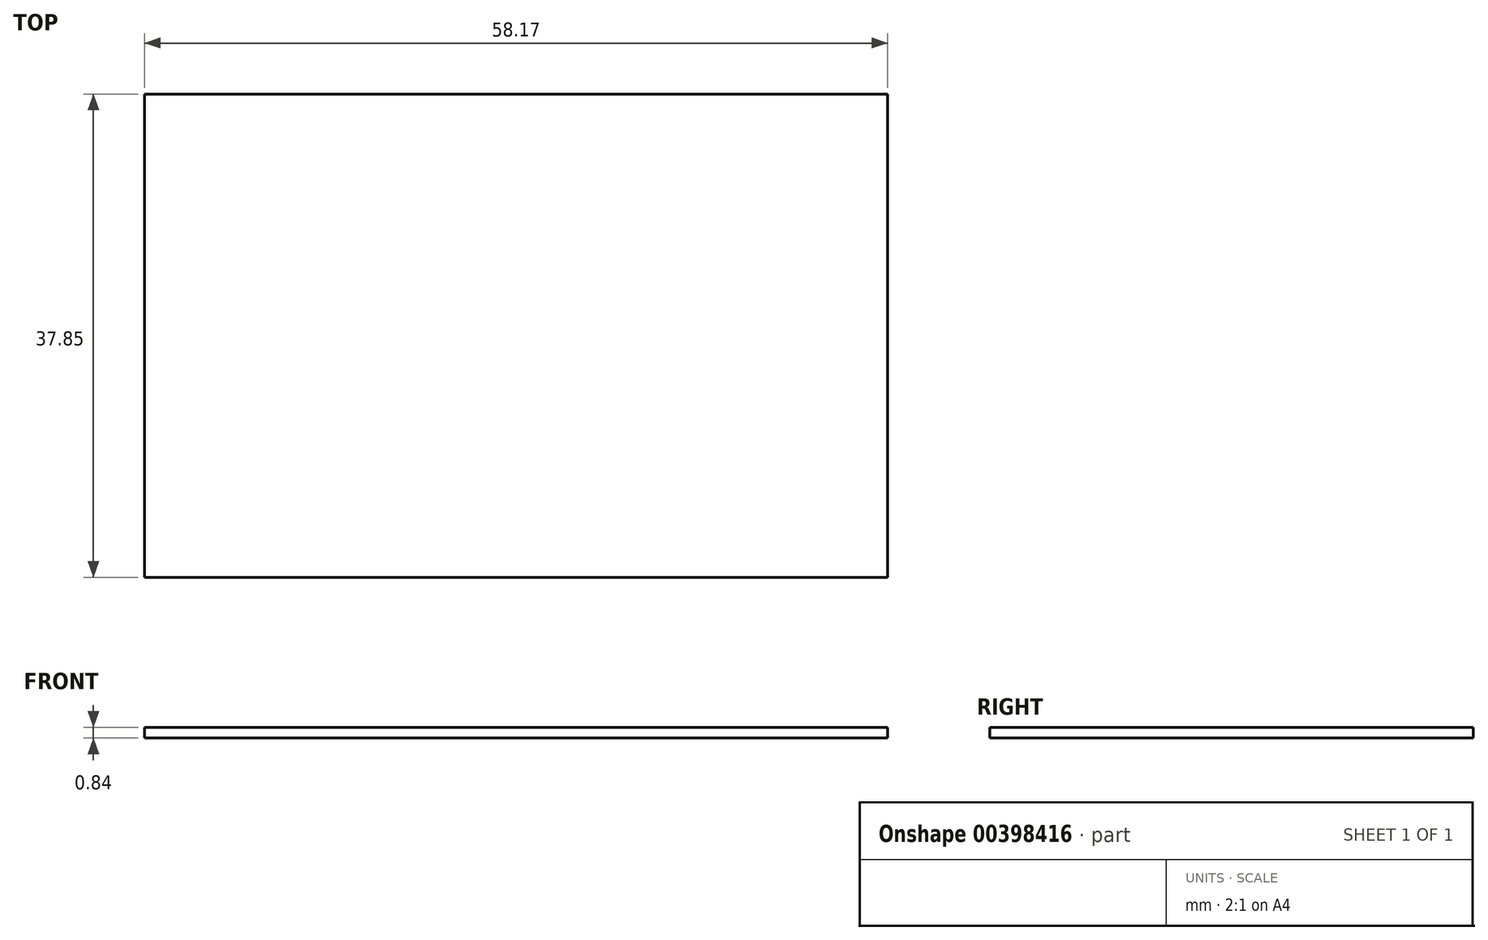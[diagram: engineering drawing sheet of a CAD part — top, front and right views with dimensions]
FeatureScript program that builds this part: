
annotation { "Feature Type Name" : "Feature", "Feature Type Description" : "" }
export const myFeature = defineFeature(function(context is Context, id is Id, definition is map)
    precondition{}
    {
        {
            var Q0;
            Q0=qCreatedBy(makeId("Top.planeOp"),FACE);
            var sketch = newSketch(context, id + "F0", { "sketchPlane" : qUnion([Q0])});
            skLineSegment(sketch, "E0.bottom", {"start": v(0, 0) * mm, "end": v(58.17, 0) * mm});
            skLineSegment(sketch, "E0.top", {"start": v(0, -37.85) * mm, "end": v(58.17, -37.85) * mm});
            skLineSegment(sketch, "E0.left", {"start": v(0, 0) * mm, "end": v(0, -37.85) * mm});
            skLineSegment(sketch, "E0.right", {"start": v(58.17, 0) * mm, "end": v(58.17, -37.85) * mm});
            skSolve(sketch);
        }
        {
            var Q0;
            Q0 = qSketchRegion(id + "F0", true);
            extrude(context, id + "F1", {"entities" : qUnion([Q0]), "depth" : 0.84 * mm});
        }
    });
